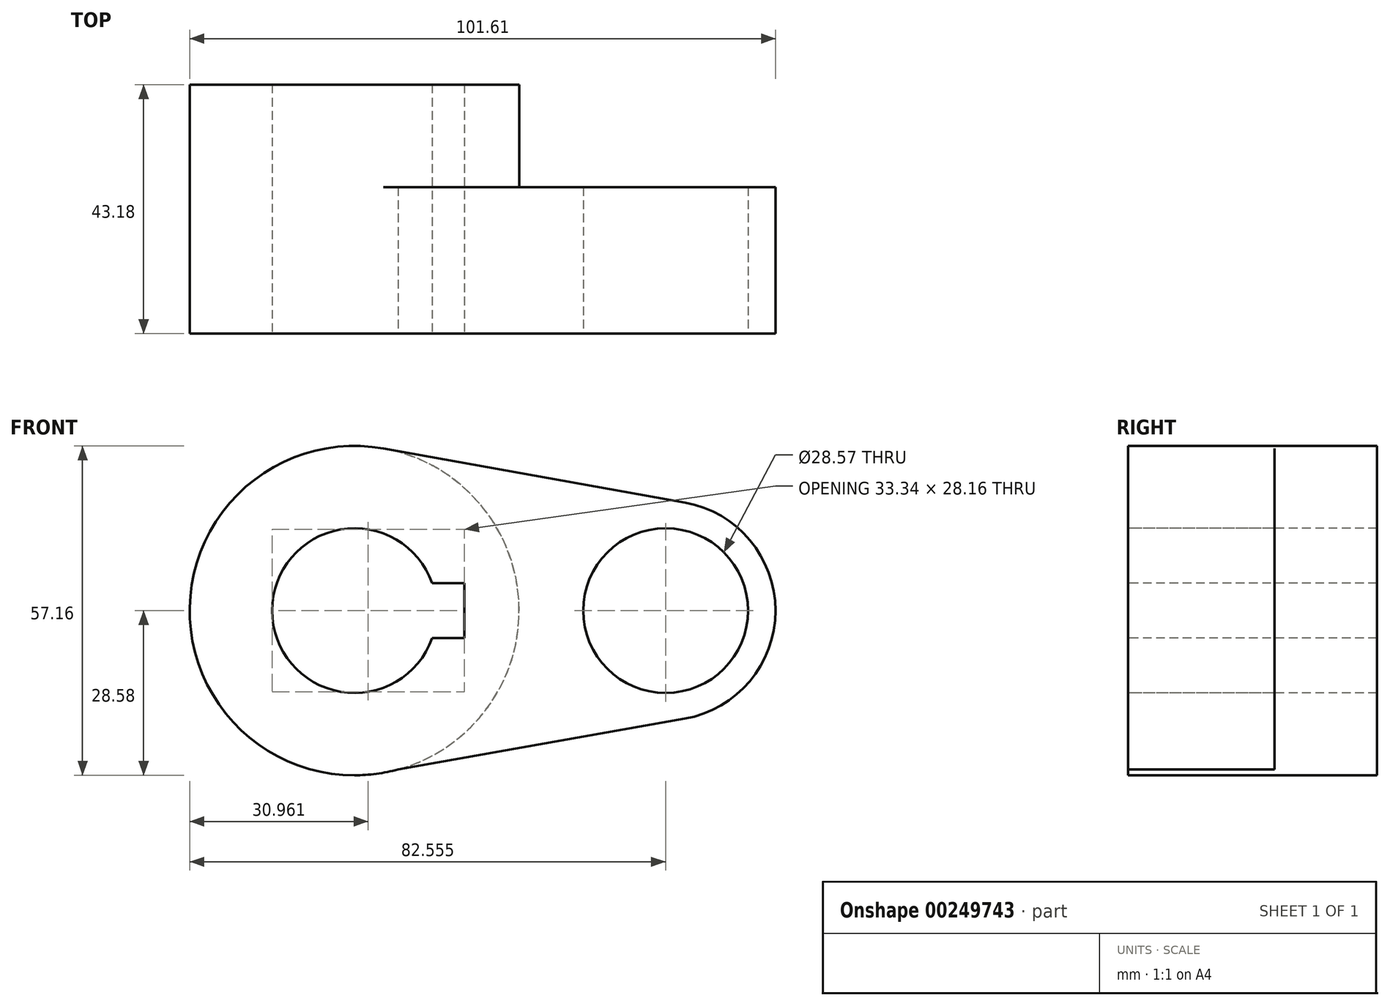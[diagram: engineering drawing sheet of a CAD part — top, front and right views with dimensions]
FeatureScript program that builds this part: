
annotation { "Feature Type Name" : "Feature", "Feature Type Description" : "" }
export const myFeature = defineFeature(function(context is Context, id is Id, definition is map)
    precondition{}
    {
        {
            var Q0;
            Q0=qCreatedBy(makeId("Front.planeOp"),FACE);
            var sketch = newSketch(context, id + "F0", { "sketchPlane" : qUnion([Q0])});
            skCircle(sketch, "E0", {"center": v(0, 0) * mm, "radius": 28.58 * mm});
            skCircle(sketch, "E1", {"center": v(53.98, 0) * mm, "radius": 19.05 * mm});
            skLineSegment(sketch, "E2", {"start": v(5.04, 28.13) * mm, "end": v(57.34, 18.75) * mm});
            skLineSegment(sketch, "E3", {"start": v(7.56, -27.56) * mm, "end": v(57.3, -18.76) * mm});
            skCircle(sketch, "E4", {"center": v(0, 0) * mm, "radius": 14.29 * mm});
            skCircle(sketch, "E5", {"center": v(53.98, 0) * mm, "radius": 14.29 * mm});
            skLineSegment(sketch, "E6.bottom", {"start": v(19.05, -4.76) * mm, "end": v(-19.05, -4.76) * mm});
            skLineSegment(sketch, "E6.top", {"start": v(19.05, 4.76) * mm, "end": v(-19.05, 4.76) * mm});
            skLineSegment(sketch, "E6.left", {"start": v(19.05, -4.76) * mm, "end": v(19.05, 4.76) * mm});
            skLineSegment(sketch, "E6.right", {"start": v(-19.05, -4.76) * mm, "end": v(-19.05, 4.76) * mm});
            skSolve(sketch);
        }
        {
            var Q0;
            Q0 = qSketchRegion(id + "F0", true);
            var Q1;
            {var subQ5=sQuery(id+"F0.wireOp",EDGE,"E6.right");Q1=makeQuery(id+"F0.imprint","IMPRINT",FACE,{"disambiguationData":[TD([[makeQuery(id+"F0.imprint","IMPRINT",EDGE,{"derivedFrom":subQ5}),-1.0]])]});}
            extrude(context, id + "F1", {"entities" : qUnion([Q0, Q1]), "oppositeDirection" : true, "depth" : 25.4 * mm});
        }
        {
            var Q0;
            {var subQ5=sQuery(id+"F0.wireOp",EDGE,"E6.right");Q0=makeQuery(id+"F0.imprint","IMPRINT",FACE,{"disambiguationData":[TD([[makeQuery(id+"F0.imprint","IMPRINT",EDGE,{"derivedFrom":subQ5}),-1.0]])]});}
            var Q1;
            {var subQ11=sQuery(id+"F0.wireOp",EDGE,"E6.left");Q1=makeQuery(id+"F0.imprint","IMPRINT",FACE,{"disambiguationData":[TD([[makeQuery(id+"F0.imprint","IMPRINT",EDGE,{"derivedFrom":subQ11}),-1.0]])]});}
            extrude(context, id + "F2", {"entities" : qUnion([Q0, Q1]), "operationType" : NewBodyOperationType.ADD, "oppositeDirection" : true, "depth" : 43.18 * mm});
        }
    });
